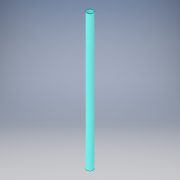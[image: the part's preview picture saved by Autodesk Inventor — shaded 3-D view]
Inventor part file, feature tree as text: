
AUTODESK INVENTOR PART (.ipt)
format: ipt  version: 2018 (Build 220112000, 112)  size: 105,472 bytes
history: native  units: in
note: dims shown in document units (in); Inventor stores cm internally (conversion verified against a paired STEP export)
features: extrude x1, sketch x1
ambient origin geometry x8: Origin, YZ Plane, XZ Plane, XY Plane, X Axis, Y Axis, Z Axis, Center Point
bodies: Solid1 (feature_tree)
feature tree (2):
  extrude  "Extrusion1"  Depth=8.164in
  sketch  "Sketch1"  dims[d0=0.375in d1=0.31in d2=8.164in d3=0.0in]
